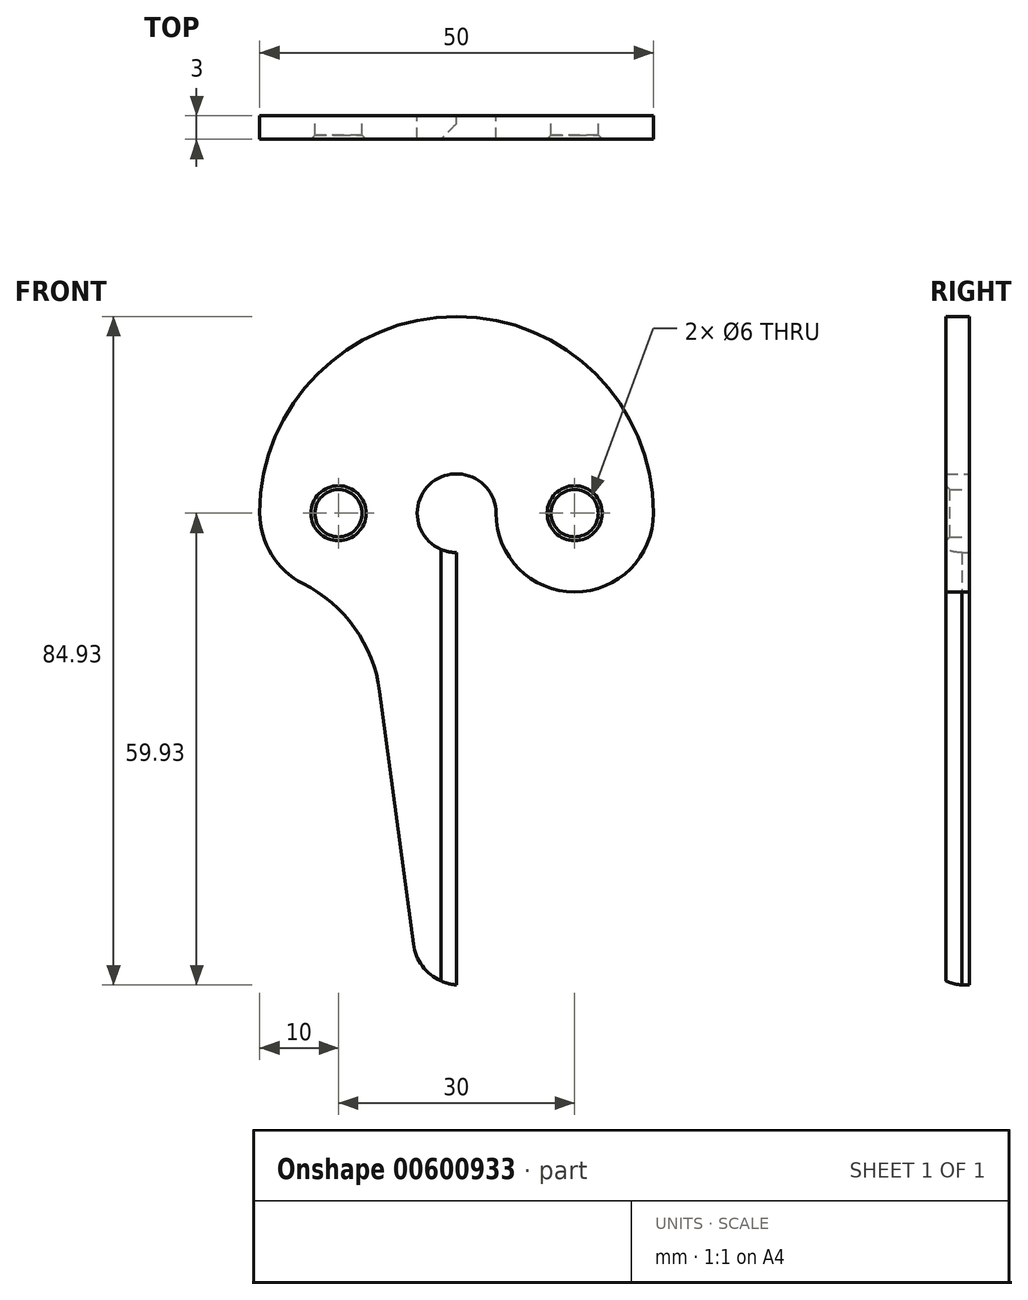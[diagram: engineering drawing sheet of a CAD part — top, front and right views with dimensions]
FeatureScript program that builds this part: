
annotation { "Feature Type Name" : "Feature", "Feature Type Description" : "" }
export const myFeature = defineFeature(function(context is Context, id is Id, definition is map)
    precondition{}
    {
        {
            var Q0;
            Q0=qCreatedBy(makeId("Front.planeOp"),FACE);
            var sketch = newSketch(context, id + "F0", { "sketchPlane" : qUnion([Q0])});
            skArc(sketch, "E0", {"start": v(25, 0) * mm, "mid": v(0, 25) * mm, "end": v(-25, 0) * mm});
            skCircle(sketch, "E1", {"center": v(-15, 0) * mm, "radius": 3 * mm});
            skCircle(sketch, "E2", {"center": v(15, 0) * mm, "radius": 3 * mm});
            skPoint(sketch, "E3", {"position": v(0, -60) * mm});
            skArc(sketch, "E4", {"start": v(-9.77, -22.62) * mm, "mid": v(-12.94, -14.57) * mm, "end": v(-19.5, -8.93) * mm});
            skArc(sketch, "E5", {"start": v(5, 0) * mm, "mid": v(-3.54, 3.54) * mm, "end": v(0, -5) * mm});
            skArc(sketch, "E6", {"start": v(5, 0) * mm, "mid": v(15, -10) * mm, "end": v(25, 0) * mm});
            skArc(sketch, "E7", {"start": v(-25, 0) * mm, "mid": v(-23.52, -5.24) * mm, "end": v(-19.5, -8.93) * mm});
            skLineSegment(sketch, "E8", {"start": v(0, -5) * mm, "end": v(0, -60) * mm});
            skArc(sketch, "E9", {"start": v(-5.5, -54.73) * mm, "mid": v(-3.55, -58.4) * mm, "end": v(0.3, -59.94) * mm});
            skPoint(sketch, "E10.center.orphan", {"position": v(0, -54) * mm});
            skLineSegment(sketch, "E11", {"start": v(-5.5, -54.73) * mm, "end": v(-9.77, -22.62) * mm});
            skSolve(sketch);
        }
        {
            var Q0;
            Q0=makeQuery(id+"F0.imprint","IMPRINT",FACE,{"disambiguationData":[TD([[makeQuery(id+"F0.imprint","IMPRINT",EDGE,{"derivedFrom":sQuery(id+"F0.wireOp",EDGE,"E0")}),1.0]])]});
            extrude(context, id + "F1", {"entities" : qUnion([Q0]), "depth" : 3 * mm});
        }
        {
            var Q0;
            Q0=makeQuery(id+"F1.opExtrude","CAP_EDGE",EDGE,{"disambiguationData":[OSD([sQuery(id+"F0.wireOp",EDGE,"E8")])],"isStart":false});
            chamfer(context, id + "F2", {"entities" : qUnion([Q0]), "width" : 2 * mm, "tangentPropagation" : true});
        }
        {
            var Q0;
            Q0=makeQuery(id+"F1.opExtrude","CAP_EDGE",EDGE,{"disambiguationData":[OSD([sQuery(id+"F0.wireOp",EDGE,"E1")])],"isStart":false});
            chamfer(context, id + "F3", {"entities" : qUnion([Q0]), "width" : 0.5 * mm, "tangentPropagation" : true});
        }
        {
            var Q0;
            Q0=makeQuery(id+"F1.opExtrude","CAP_EDGE",EDGE,{"disambiguationData":[OSD([sQuery(id+"F0.wireOp",EDGE,"E2")])],"isStart":false});
            chamfer(context, id + "F4", {"entities" : qUnion([Q0]), "width" : 0.5 * mm, "tangentPropagation" : true});
        }
    });
